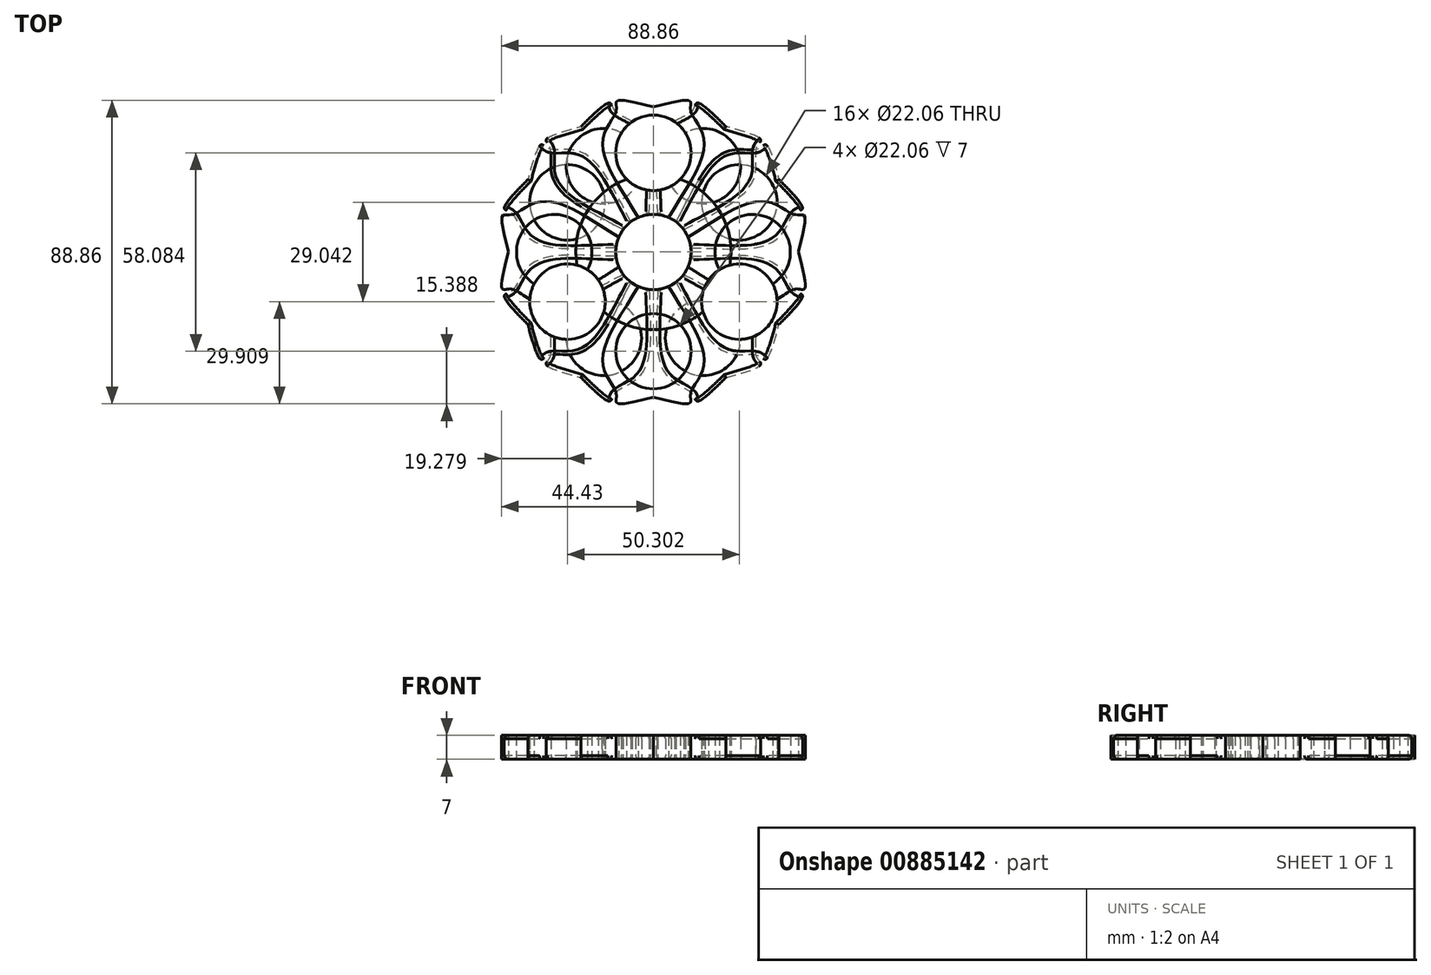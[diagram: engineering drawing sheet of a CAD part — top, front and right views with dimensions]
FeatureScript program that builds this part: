
annotation { "Feature Type Name" : "Feature", "Feature Type Description" : "" }
export const myFeature = defineFeature(function(context is Context, id is Id, definition is map)
    precondition{}
    {
        {
            var Q0;
            Q0=qCreatedBy(makeId("Top.planeOp"),FACE);
            var sketch = newSketch(context, id + "F0", { "sketchPlane" : qUnion([Q0])});
            skCircle(sketch, "E0", {"center": v(0, 0) * mm, "radius": 11.03 * mm});
            skCircle(sketch, "E1", {"center": v(0, 29.04) * mm, "radius": 11.03 * mm});
            skSolve(sketch);
        }
        {
            var Q0;
            Q0=qCreatedBy(makeId("Top.planeOp"),FACE);
            var sketch = newSketch(context, id + "F1", { "sketchPlane" : qUnion([Q0])});
            skLineSegment(sketch, "E2", {"start": v(0, 0) * mm, "end": v(0, 42.42) * mm});
            skFitSpline(sketch, "E3", {"points": [v(0, 42.42) * mm, v(-10.8, 41.93) * mm, v(-13.88, 35.9) * mm, v(-12.93, 24.45) * mm, v(0, 0) * mm, v(-168.53, 57.38) * mm], "startDerivative": vector(-341.35, 90.7) * mm, "endDerivative": vector(-685.05, 278.66) * mm});
            skFitSpline(sketch, "E4.MirrorCS", {"points": [v(0, 42.42) * mm, v(10.8, 41.93) * mm, v(13.88, 35.9) * mm, v(12.93, 24.45) * mm, v(0, 0) * mm, v(168.53, 57.38) * mm], "startDerivative": vector(341.35, 90.7) * mm, "endDerivative": vector(685.05, 278.66) * mm});
            skLineSegment(sketch, "E5.1.0", {"start": v(0, 0) * mm, "end": v(-36.74, -21.21) * mm});
            skLineSegment(sketch, "E5.2.0", {"start": v(0, 0) * mm, "end": v(36.74, -21.21) * mm});
            skSolve(sketch);
        }
        {
            var Q0;
            Q0=qCreatedBy(makeId("Front.planeOp"),FACE);
            var sketch = newSketch(context, id + "F2", { "sketchPlane" : qUnion([Q0])});
            skLineSegment(sketch, "E6", {"start": v(0, 0) * mm, "end": v(0, 34.06) * mm});
            skLineSegment(sketch, "E7", {"start": v(0, 34.06) * mm, "end": v(0, 0) * mm, "construction": true});
            skSolve(sketch);
        }
        {
            var Q0;
            Q0=makeQuery(id+"F1.imprint","IMPRINT",FACE,{"disambiguationData":[TD([[makeQuery(id+"F1.imprint","IMPRINT",EDGE,{"derivedFrom":sQuery(id+"F1.wireOp",EDGE,"E2")}),1.0]])]});
            var Q1;
            Q1=makeQuery(id+"F1.imprint","IMPRINT",FACE,{"disambiguationData":[TD([[makeQuery(id+"F1.imprint","IMPRINT",EDGE,{"derivedFrom":sQuery(id+"F1.wireOp",EDGE,"E2")}),-1.0]])]});
            extrude(context, id + "F3", {"entities" : qUnion([Q0, Q1]), "depth" : 7 * mm, "offsetDistance" : 25 * mm});
        }
        {
            var Q0;
            Q0=makeQuery(id+"F0.imprint","IMPRINT",FACE,{"disambiguationData":[TD([[makeQuery(id+"F0.imprint","IMPRINT",EDGE,{"derivedFrom":sQuery(id+"F0.wireOp",EDGE,"E1")}),1.0]])]});
            extrude(context, id + "F4", {"entities" : qUnion([Q0]), "operationType" : NewBodyOperationType.REMOVE, "depth" : 96.9 * mm, "offsetDistance" : 25 * mm});
        }
        {
            var Q0;
            Q0=makeQuery(id+"F3.opExtrude","SWEPT_BODY",BODY,{"disambiguationData":[OSD([sQuery(id+"F1.wireOp",EDGE,"E3"),sQuery(id+"F1.wireOp",EDGE,"E4.MirrorCS")])]});
            var Q1;
            Q1=sQuery(id+"F2.wireOp",EDGE,"E6");
            circularPattern(context, id + "F5", {"entities" : qUnion([Q0]), "axis" : qUnion([Q1]), "angle" : 360 * degree, "instanceCount" : 3, "equalSpace" : true});
        }
        {
            var Q0;
            Q0=qCreatedBy(makeId("Top.planeOp"),FACE);
            var sketch = newSketch(context, id + "F6", { "sketchPlane" : qUnion([Q0])});
            skCircle(sketch, "E8", {"center": v(0, 0) * mm, "radius": 22.73 * mm});
            skCircle(sketch, "E9", {"center": v(0, 0) * mm, "radius": 17.15 * mm});
            skSolve(sketch);
        }
        {
            var Q0;
            Q0 = qSketchRegion(id + "F6", true);
            var Q1;
            Q1=makeQuery(id+"F6.imprint","IMPRINT",FACE,{"disambiguationData":[TD([[makeQuery(id+"F6.imprint","IMPRINT",EDGE,{"derivedFrom":sQuery(id+"F6.wireOp",EDGE,"E9")}),1.0]])]});
            var Q2;
            Q2=makeQuery(id+"F0.imprint","IMPRINT",FACE,{"disambiguationData":[TD([[makeQuery(id+"F0.imprint","IMPRINT",EDGE,{"derivedFrom":sQuery(id+"F0.wireOp",EDGE,"E0")}),1.0]])]});
            extrude(context, id + "F7", {"entities" : qUnion([Q0, Q1, Q2]), "depth" : 7 * mm, "offsetDistance" : 25 * mm});
        }
        {
            var Q0;
            Q0=makeQuery(id+"F0.imprint","IMPRINT",FACE,{"disambiguationData":[TD([[makeQuery(id+"F0.imprint","IMPRINT",EDGE,{"derivedFrom":sQuery(id+"F0.wireOp",EDGE,"E0")}),1.0]])]});
            extrude(context, id + "F8", {"entities" : qUnion([Q0]), "operationType" : NewBodyOperationType.REMOVE, "depth" : 118.2 * mm, "offsetDistance" : 25 * mm});
        }
        {
            var Q0;
            Q0=makeQuery(id+"F5.opPattern","COPY",FACE,{"derivedFrom":makeQuery(id+"F3.opExtrude","CAP_FACE",FACE,{"disambiguationData":[OSD([sQuery(id+"F1.wireOp",EDGE,"E3"),sQuery(id+"F1.wireOp",EDGE,"E4.MirrorCS")])],"isStart":false}),"instanceName":"1"});
            var Q1;
            Q1=makeQuery(id+"F3.opExtrude","CAP_EDGE",EDGE,{"disambiguationData":[OSD([sQuery(id+"F1.wireOp",EDGE,"E4.MirrorCS")])],"isStart":false});
            var Q2;
            Q2=makeQuery(id+"F5.opPattern","COPY",FACE,{"derivedFrom":makeQuery(id+"F3.opExtrude","CAP_FACE",FACE,{"disambiguationData":[OSD([sQuery(id+"F1.wireOp",EDGE,"E3"),sQuery(id+"F1.wireOp",EDGE,"E4.MirrorCS")])],"isStart":false}),"instanceName":"2"});
            var Q3;
            Q3=makeQuery(id+"F5.opPattern","COPY",FACE,{"derivedFrom":makeQuery(id+"F3.opExtrude","CAP_FACE",FACE,{"disambiguationData":[OSD([sQuery(id+"F1.wireOp",EDGE,"E3"),sQuery(id+"F1.wireOp",EDGE,"E4.MirrorCS")])],"isStart":true}),"instanceName":"1"});
            var Q4;
            Q4=makeQuery(id+"F3.opExtrude","CAP_FACE",FACE,{"disambiguationData":[OSD([sQuery(id+"F1.wireOp",EDGE,"E3"),sQuery(id+"F1.wireOp",EDGE,"E4.MirrorCS")])],"isStart":true});
            var Q5;
            Q5=makeQuery(id+"F5.opPattern","COPY",FACE,{"derivedFrom":makeQuery(id+"F3.opExtrude","CAP_FACE",FACE,{"disambiguationData":[OSD([sQuery(id+"F1.wireOp",EDGE,"E3"),sQuery(id+"F1.wireOp",EDGE,"E4.MirrorCS")])],"isStart":true}),"instanceName":"2"});
            fillet(context, id + "F9", {"entities" : qUnion([Q0, Q1, Q2, Q3, Q4, Q5]), "radius" : 1 * mm, "tangentPropagation" : true, "allowEdgeOverflow" : false});
        }
        {
            var Q0;
            Q0=makeQuery(id+"F3.opExtrude","SWEPT_BODY",BODY,{"disambiguationData":[OSD([sQuery(id+"F1.wireOp",EDGE,"E3"),sQuery(id+"F1.wireOp",EDGE,"E4.MirrorCS")])]});
            var Q1;
            Q1=makeQuery(id+"F5.opPattern","COPY",BODY,{"derivedFrom":makeQuery(id+"F3.opExtrude","SWEPT_BODY",BODY,{"disambiguationData":[OSD([sQuery(id+"F1.wireOp",EDGE,"E3"),sQuery(id+"F1.wireOp",EDGE,"E4.MirrorCS")])]}),"instanceName":"1"});
            var Q2;
            Q2=makeQuery(id+"F5.opPattern","COPY",BODY,{"derivedFrom":makeQuery(id+"F3.opExtrude","SWEPT_BODY",BODY,{"disambiguationData":[OSD([sQuery(id+"F1.wireOp",EDGE,"E3"),sQuery(id+"F1.wireOp",EDGE,"E4.MirrorCS")])]}),"instanceName":"2"});
            var Q3;
            Q3=makeQuery(id+"F7.opExtrude","SWEPT_BODY",BODY,{"disambiguationData":[OSD([sQuery(id+"F6.wireOp",EDGE,"E8")])]});
            var Q4;
            Q4=sQuery(id+"F2.wireOp",EDGE,"E6");
            circularPattern(context, id + "F10", {"entities" : qUnion([Q0, Q1, Q2, Q3]), "axis" : qUnion([Q4]), "angle" : 360 * degree, "instanceCount" : 4, "equalSpace" : true});
        }
        {
            var Q0;
            Q0=qCreatedBy(makeId("Top.planeOp"),FACE);
            var sketch = newSketch(context, id + "F11", { "sketchPlane" : qUnion([Q0])});
            skCircle(sketch, "E10.0", {"center": v(-25.15, -14.52) * mm, "radius": 11.03 * mm});
            skCircle(sketch, "E10.1", {"center": v(0, 29.04) * mm, "radius": 11.03 * mm});
            skCircle(sketch, "E10.2", {"center": v(25.15, -14.52) * mm, "radius": 11.03 * mm});
            skSolve(sketch);
        }
        {
            var Q0;
            Q0 = qSketchRegion(id + "F11", true);
            extrude(context, id + "F12", {"entities" : qUnion([Q0]), "operationType" : NewBodyOperationType.REMOVE, "depth" : 69.3 * mm, "offsetDistance" : 25 * mm});
        }
    });
